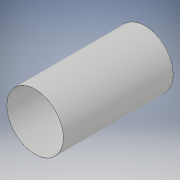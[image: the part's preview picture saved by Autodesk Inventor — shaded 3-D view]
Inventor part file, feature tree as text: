
AUTODESK INVENTOR PART (.ipt)
format: ipt  version: 2019 (Build 230136000, 136)  size: 98,816 bytes
history: native  units: mm
features: extrude x2, sketch x2
ambient origin geometry x8: Origin, YZ Plane, XZ Plane, XY Plane, X Axis, Y Axis, Z Axis, Center Point
bodies: Solid1 (feature_tree)
feature tree (4):
  extrude  "Extrusion1"  Depth=192.675mm TaperAngle=0.0deg
  extrude  "Extrusion2"  Depth=192.675mm TaperAngle=0.0deg
  sketch  "Sketch1"  dims[d0=99.2mm d1=192.675mm d2=0.0mm]
  sketch  "Sketch2"  dims[d3=98.9mm d4=192.675mm d5=0.0mm]
